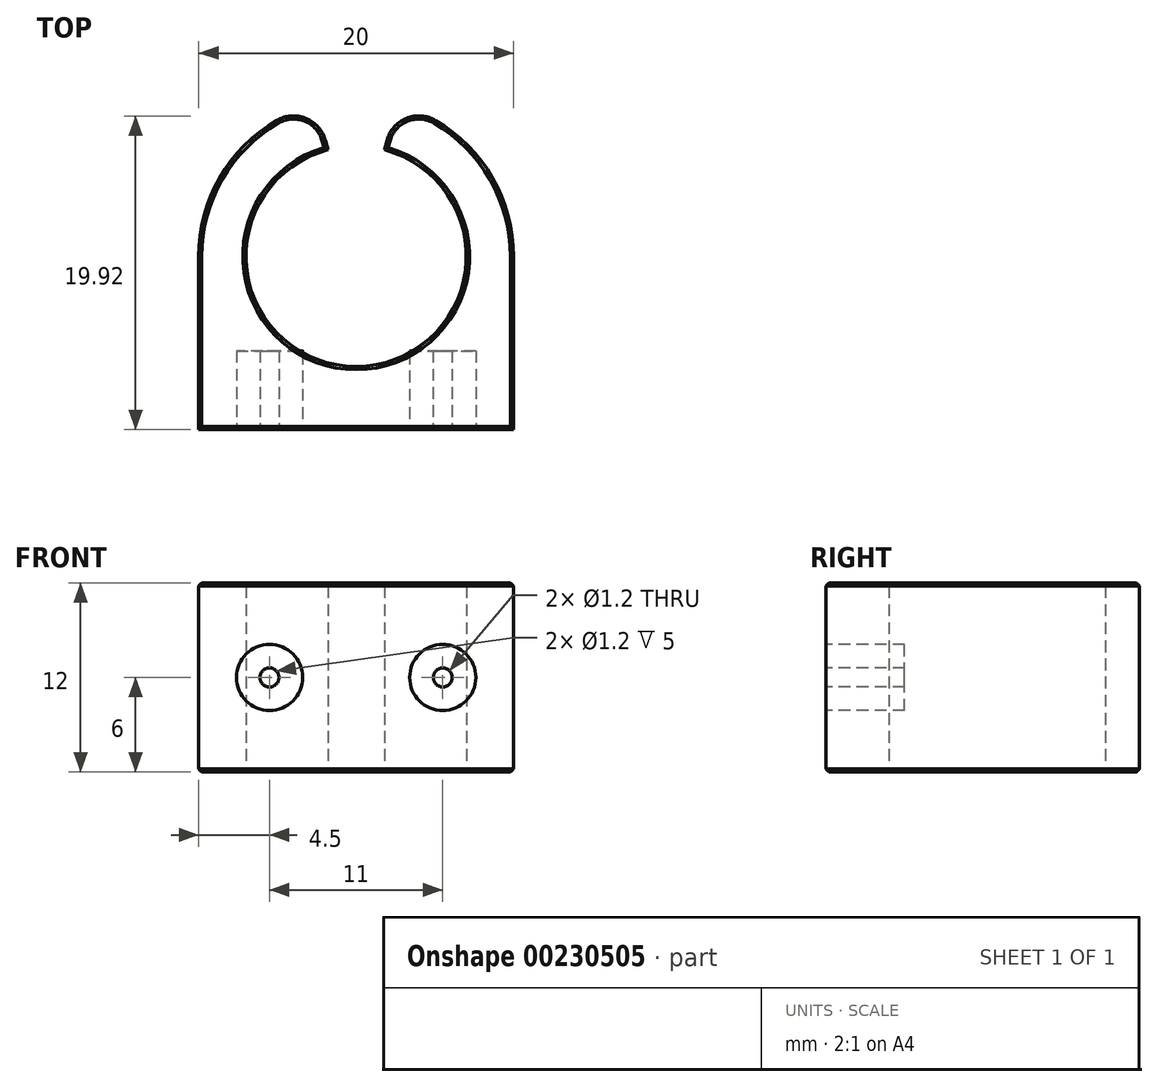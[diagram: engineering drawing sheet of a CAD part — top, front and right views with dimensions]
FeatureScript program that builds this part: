
annotation { "Feature Type Name" : "Feature", "Feature Type Description" : "" }
export const myFeature = defineFeature(function(context is Context, id is Id, definition is map)
    precondition{}
    {
        {
            var Q0;
            Q0=qCreatedBy(makeId("Top.planeOp"),FACE);
            var sketch = newSketch(context, id + "F0", { "sketchPlane" : qUnion([Q0])});
            skLineSegment(sketch, "E0.top", {"start": v(-10, -11) * mm, "end": v(10, -11) * mm});
            skLineSegment(sketch, "E0.left", {"start": v(-10, 0) * mm, "end": v(-10, -11) * mm});
            skLineSegment(sketch, "E0.right", {"start": v(10, 0) * mm, "end": v(10, -11) * mm});
            skArc(sketch, "E1.0", {"start": v(10, 0) * mm, "mid": v(8.67, 4.98) * mm, "end": v(5.04, 8.63) * mm});
            skPoint(sketch, "E2.visualSharp", {"position": v(-7, 0.2) * mm});
            skPoint(sketch, "E3.visualSharp", {"position": v(-7, -0.2) * mm});
            skArc(sketch, "E4", {"start": v(-1.8, 6.77) * mm, "mid": v(0, -7) * mm, "end": v(1.8, 6.77) * mm});
            skLineSegment(sketch, "E5", {"start": v(1.8, 6.77) * mm, "end": v(1.96, 7.36) * mm});
            skLineSegment(sketch, "E6.MirrorCS", {"start": v(-1.8, 6.77) * mm, "end": v(-1.96, 7.36) * mm});
            skPoint(sketch, "E7.orphan", {"position": v(3.14, 11.83) * mm});
            skPoint(sketch, "E8.orphan", {"position": v(-3.14, 11.83) * mm});
            skArc(sketch, "E9.trimOffspring", {"start": v(-5.04, 8.63) * mm, "mid": v(-8.67, 4.98) * mm, "end": v(-10, 0) * mm});
            skPoint(sketch, "E10.visualSharp", {"position": v(-2.57, 9.66) * mm});
            skArc(sketch, "E10.filletArc", {"start": v(-1.96, 7.36) * mm, "mid": v(-3.18, 8.76) * mm, "end": v(-5.04, 8.63) * mm});
            skPoint(sketch, "E11.visualSharp", {"position": v(2.57, 9.66) * mm});
            skArc(sketch, "E11.filletArc", {"start": v(5.04, 8.63) * mm, "mid": v(3.18, 8.76) * mm, "end": v(1.96, 7.36) * mm});
            skSolve(sketch);
        }
        {
            var Q0;
            Q0=qSketchRegion(id+"F0",true);
            extrude(context, id + "F1", {"entities" : qUnion([Q0]), "depth" : 12 * mm});
        }
        {
            var Q0;
            Q0=makeQuery(id+"F1.opExtrude","SWEPT_FACE",FACE,{"disambiguationData":[OSD([sQuery(id+"F0.wireOp",EDGE,"E0.top")])]});
            var sketch = newSketch(context, id + "F2", { "sketchPlane" : qUnion([Q0])});
            skCircle(sketch, "E12", {"center": v(-5.5, 6) * mm, "radius": 0.6 * mm});
            skCircle(sketch, "E13.MirrorC", {"center": v(5.5, 6) * mm, "radius": 0.6 * mm});
            skSolve(sketch);
        }
        {
            var Q0;
            Q0=qSketchRegion(id+"F2",true);
            extrude(context, id + "F3", {"entities" : qUnion([Q0]), "operationType" : NewBodyOperationType.REMOVE, "oppositeDirection" : true, "depth" : 5 * mm});
        }
        {
            var Q0;
            Q0=makeQuery(id+"F1.opExtrude","SWEPT_FACE",FACE,{"disambiguationData":[OSD([sQuery(id+"F0.wireOp",EDGE,"E0.top")])]});
            var sketch = newSketch(context, id + "F4", { "sketchPlane" : qUnion([Q0])});
            skCircle(sketch, "E14.0", {"center": v(-5.5, 6) * mm, "radius": 2.1 * mm});
            skCircle(sketch, "E15.0", {"center": v(5.5, 6) * mm, "radius": 2.1 * mm});
            skCircle(sketch, "E16.0", {"center": v(-5.5, 6) * mm, "radius": 0.6 * mm});
            skCircle(sketch, "E17.0", {"center": v(5.5, 6) * mm, "radius": 0.6 * mm});
            skSolve(sketch);
        }
        {
            var Q0;
            Q0=makeQuery(id+"F4.imprint","IMPRINT",FACE,{"disambiguationData":[TD([[makeQuery(id+"F4.imprint","IMPRINT",EDGE,{"derivedFrom":sQuery(id+"F4.wireOp",EDGE,"E15.0")}),1.0]])]});
            var Q1;
            Q1=makeQuery(id+"F4.imprint","IMPRINT",FACE,{"disambiguationData":[TD([[makeQuery(id+"F4.imprint","IMPRINT",EDGE,{"derivedFrom":sQuery(id+"F4.wireOp",EDGE,"E14.0")}),1.0]])]});
            extrude(context, id + "F5", {"entities" : qUnion([Q0, Q1]), "oppositeDirection" : true, "depth" : 5 * mm});
        }
        {
            var Q0;
            Q0=makeQuery(id+"F1.opExtrude","CAP_EDGE",EDGE,{"disambiguationData":[OSD([sQuery(id+"F0.wireOp",EDGE,"E4")])],"isStart":false});
            var Q1;
            Q1=makeQuery(id+"F1.opExtrude","CAP_EDGE",EDGE,{"disambiguationData":[OSD([sQuery(id+"F0.wireOp",EDGE,"E6.MirrorCS")])],"isStart":false});
            var Q2;
            Q2=makeQuery(id+"F1.opExtrude","CAP_EDGE",EDGE,{"disambiguationData":[OSD([sQuery(id+"F0.wireOp",EDGE,"E10.filletArc")])],"isStart":false});
            var Q3;
            Q3=makeQuery(id+"F1.opExtrude","CAP_EDGE",EDGE,{"disambiguationData":[OSD([sQuery(id+"F0.wireOp",EDGE,"E0.top")])],"isStart":false});
            var Q4;
            Q4=makeQuery(id+"F1.opExtrude","CAP_FACE",FACE,{"disambiguationData":[OSD([sQuery(id+"F0.wireOp",EDGE,"E0.top"),sQuery(id+"F0.wireOp",EDGE,"E0.left"),sQuery(id+"F0.wireOp",EDGE,"E0.right"),sQuery(id+"F0.wireOp",EDGE,"E1.0"),sQuery(id+"F0.wireOp",EDGE,"E4"),sQuery(id+"F0.wireOp",EDGE,"E5"),sQuery(id+"F0.wireOp",EDGE,"E6.MirrorCS"),sQuery(id+"F0.wireOp",EDGE,"E9.trimOffspring"),sQuery(id+"F0.wireOp",EDGE,"E10.filletArc"),sQuery(id+"F0.wireOp",EDGE,"E11.filletArc")])],"isStart":false});
            chamfer(context, id + "F6", {"entities" : qUnion([Q0, Q1, Q2, Q3, Q4]), "width" : 0.2 * mm, "tangentPropagation" : true});
        }
        {
            var Q0;
            Q0=makeQuery(id+"F1.opExtrude","CAP_FACE",FACE,{"disambiguationData":[OSD([sQuery(id+"F0.wireOp",EDGE,"E0.top"),sQuery(id+"F0.wireOp",EDGE,"E0.left"),sQuery(id+"F0.wireOp",EDGE,"E0.right"),sQuery(id+"F0.wireOp",EDGE,"E1.0"),sQuery(id+"F0.wireOp",EDGE,"E4"),sQuery(id+"F0.wireOp",EDGE,"E5"),sQuery(id+"F0.wireOp",EDGE,"E6.MirrorCS"),sQuery(id+"F0.wireOp",EDGE,"E9.trimOffspring"),sQuery(id+"F0.wireOp",EDGE,"E10.filletArc"),sQuery(id+"F0.wireOp",EDGE,"E11.filletArc")])],"isStart":true});
            chamfer(context, id + "F7", {"entities" : qUnion([Q0]), "width" : 0.2 * mm, "tangentPropagation" : true});
        }
    });
